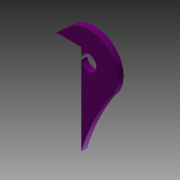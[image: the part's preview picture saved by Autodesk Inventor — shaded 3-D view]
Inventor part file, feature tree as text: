
AUTODESK INVENTOR PART (.ipt)
format: ipt  version: 2015 (Build 190159000, 159)  size: 87,040 bytes
history: native  units: mm
features: extrude x1, sketch x1
ambient origin geometry x8: Origin, YZ Plane, XZ Plane, XY Plane, X Axis, Y Axis, Z Axis, Center Point
bodies: Body1 (feature_tree)
feature tree (2):
  extrude  "Extrusion2"  [1 undecoded]
  sketch  "Sketch1"  dims[d3=2.5mm d4=0.0mm]
note: 1 required parameter value undecoded (feature->parameter linkage not recoverable at this tier; creation-order binding heuristic only, values carry confidence <= 0.55)
